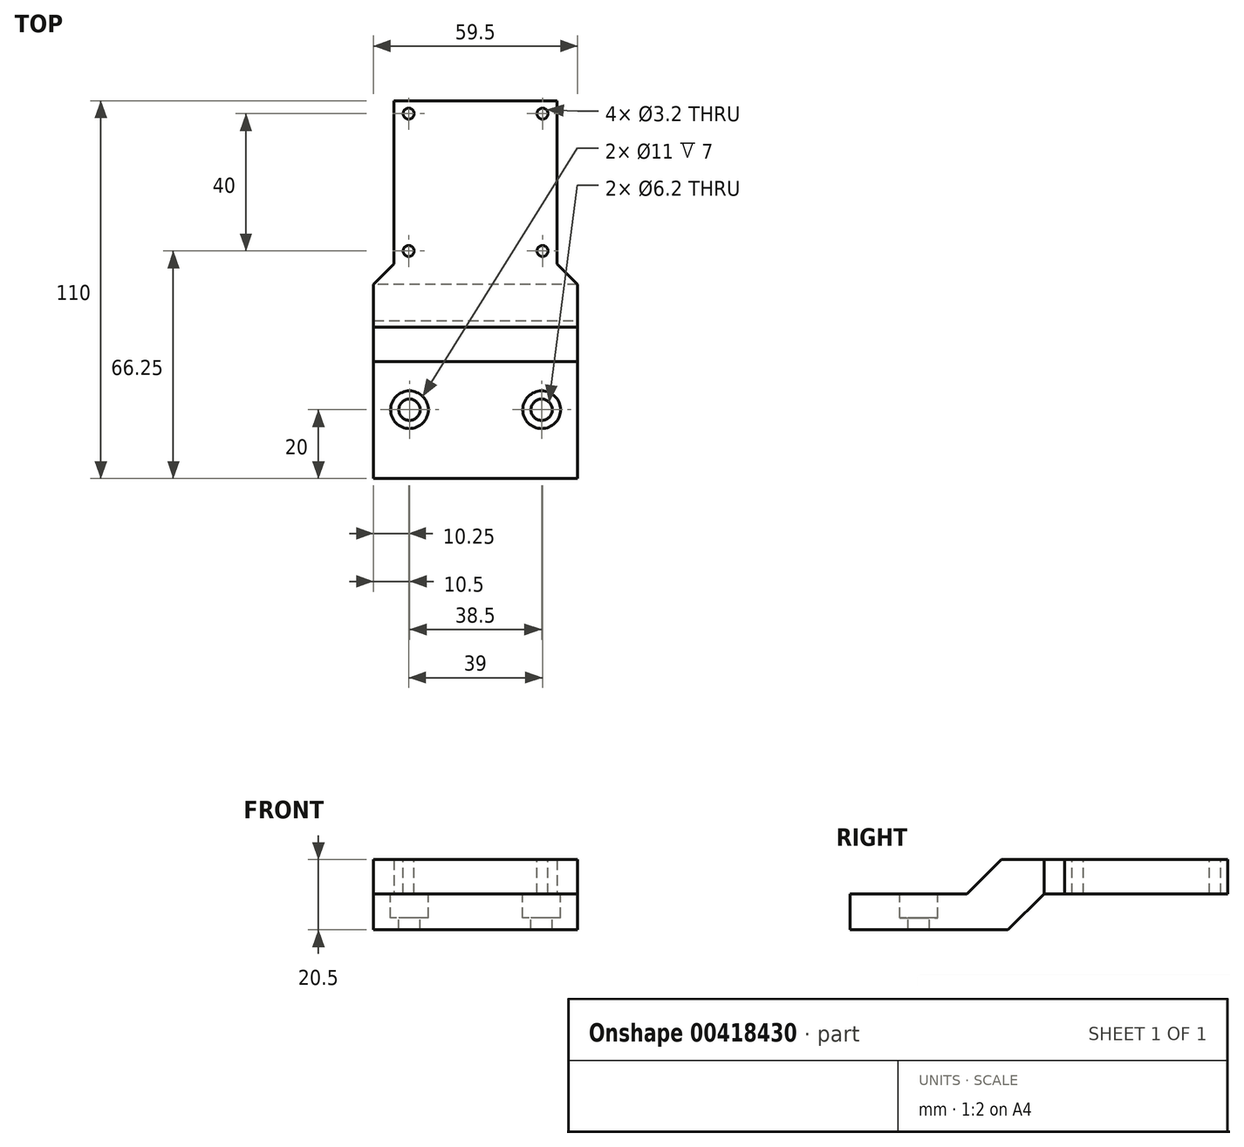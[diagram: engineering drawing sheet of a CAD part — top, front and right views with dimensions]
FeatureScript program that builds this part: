
annotation { "Feature Type Name" : "Feature", "Feature Type Description" : "" }
export const myFeature = defineFeature(function(context is Context, id is Id, definition is map)
    precondition{}
    {
        {
            var Q0;
            Q0=qCreatedBy(makeId("Top.planeOp"),FACE);
            var sketch = newSketch(context, id + "F0", { "sketchPlane" : qUnion([Q0])});
            skLineSegment(sketch, "E0.bottom", {"start": v(23.75, 23.75) * mm, "end": v(-23.75, 23.75) * mm});
            skLineSegment(sketch, "E0.left", {"start": v(23.75, 23.75) * mm, "end": v(23.75, -23.75) * mm});
            skLineSegment(sketch, "E0.right", {"start": v(-23.75, 23.75) * mm, "end": v(-23.75, -23.75) * mm});
            skPoint(sketch, "E0.middle", {"position": v(0, 0) * mm});
            skLineSegment(sketch, "E1.top", {"start": v(-29.75, -86.25) * mm, "end": v(29.75, -86.25) * mm});
            skLineSegment(sketch, "E1.left", {"start": v(-29.75, -29.75) * mm, "end": v(-29.75, -86.25) * mm});
            skLineSegment(sketch, "E1.right", {"start": v(29.75, -29.75) * mm, "end": v(29.75, -86.25) * mm});
            skLineSegment(sketch, "E2", {"start": v(-23.75, -23.75) * mm, "end": v(-29.75, -29.75) * mm});
            skLineSegment(sketch, "E3", {"start": v(23.75, -23.75) * mm, "end": v(29.75, -29.75) * mm});
            skPoint(sketch, "E4.orphan", {"position": v(-29.75, -23.75) * mm});
            skSolve(sketch);
        }
        {
            var Q0;
            Q0 = qSketchRegion(id + "F0", true);
            extrude(context, id + "F1", {"entities" : qUnion([Q0]), "depth" : 10 * mm});
        }
        {
            var Q0;
            Q0=makeQuery(id+"F1.opExtrude","CAP_FACE",FACE,{"disambiguationData":[OSD([sQuery(id+"F0.wireOp",EDGE,"E0.bottom"),sQuery(id+"F0.wireOp",EDGE,"E0.left"),sQuery(id+"F0.wireOp",EDGE,"E0.right"),sQuery(id+"F0.wireOp",EDGE,"E1.top"),sQuery(id+"F0.wireOp",EDGE,"E1.left"),sQuery(id+"F0.wireOp",EDGE,"E1.right"),sQuery(id+"F0.wireOp",EDGE,"E2"),sQuery(id+"F0.wireOp",EDGE,"E3")])],"isStart":true});
            var sketch = newSketch(context, id + "F2", { "sketchPlane" : qUnion([Q0])});
            skLineSegment(sketch, "E5", {"start": v(29.75, 86.25) * mm, "end": v(29.75, 29.75) * mm});
            skLineSegment(sketch, "E6", {"start": v(29.75, 29.75) * mm, "end": v(-29.75, 29.75) * mm});
            skLineSegment(sketch, "E7", {"start": v(-29.75, 29.75) * mm, "end": v(-29.75, 86.25) * mm});
            skLineSegment(sketch, "E8", {"start": v(-29.75, 86.25) * mm, "end": v(29.75, 86.25) * mm});
            skSolve(sketch);
        }
        {
            var Q0;
            Q0 = qSketchRegion(id + "F2", true);
            extrude(context, id + "F3", {"entities" : qUnion([Q0]), "operationType" : NewBodyOperationType.ADD, "depth" : 10.5 * mm});
        }
        {
            var Q0;
            Q0=makeQuery(id+"F3.boolean.opBoolean","MERGE",FACE,{"derivedFrom":[makeQuery(id+"F1.opExtrude","SWEPT_FACE",FACE,{"disambiguationData":[OSD([sQuery(id+"F0.wireOp",EDGE,"E1.right")])]}),makeQuery(id+"F3.opExtrude","SWEPT_FACE",FACE,{"disambiguationData":[OSD([sQuery(id+"F2.wireOp",EDGE,"E5")])]})]});
            var sketch = newSketch(context, id + "F4", { "sketchPlane" : qUnion([Q0])});
            skLineSegment(sketch, "E9", {"start": v(-42.25, 10) * mm, "end": v(-52.25, 0) * mm});
            skLineSegment(sketch, "E10", {"start": v(-52.25, 0) * mm, "end": v(-86.25, 0) * mm});
            skLineSegment(sketch, "E11", {"start": v(-86.25, 0) * mm, "end": v(-86.25, 10) * mm});
            skLineSegment(sketch, "E12", {"start": v(-29.75, 0) * mm, "end": v(-40.25, -10.5) * mm});
            skLineSegment(sketch, "E13", {"start": v(-40.25, -10.5) * mm, "end": v(-29.75, -10.5) * mm});
            skLineSegment(sketch, "E14", {"start": v(-29.75, -10.5) * mm, "end": v(-29.75, 0) * mm});
            skSolve(sketch);
        }
        {
            var Q0;
            {var subQ0=sQuery(id+"F4.wireOp",EDGE,"E9");Q0=makeQuery(id+"F4.imprint","IMPRINT",FACE,{"disambiguationData":[TD([[makeQuery(id+"F4.imprint","IMPRINT",EDGE,{"derivedFrom":subQ0}),-1.0]])]});}
            var Q1;
            Q1=makeQuery(id+"F4.imprint","IMPRINT",FACE,{"disambiguationData":[TD([[makeQuery(id+"F4.imprint","IMPRINT",EDGE,{"derivedFrom":sQuery(id+"F4.wireOp",EDGE,"E12")}),1.0]])]});
            extrude(context, id + "F5", {"entities" : qUnion([Q0, Q1]), "operationType" : NewBodyOperationType.REMOVE, "endBound" : BoundingType.THROUGH_ALL, "oppositeDirection" : true, "depth" : 25 * mm});
        }
        {
            var Q0;
            Q0=makeQuery(id+"F5.boolean.opBoolean","COPY",FACE,{"derivedFrom":makeQuery(id+"F5.opExtrude","SWEPT_FACE",FACE,{"disambiguationData":[OSD([sQuery(id+"F4.wireOp",EDGE,"E10")])]})});
            var sketch = newSketch(context, id + "F6", { "sketchPlane" : qUnion([Q0])});
            skLineSegment(sketch, "E15", {"start": v(-29.75, -66.25) * mm, "end": v(29.75, -66.25) * mm});
            skCircle(sketch, "E16", {"center": v(-19.25, -66.25) * mm, "radius": 5.5 * mm});
            skCircle(sketch, "E17", {"center": v(19.25, -66.25) * mm, "radius": 5.5 * mm});
            skSolve(sketch);
        }
        {
            var Q0;
            Q0 = qSketchRegion(id + "F6", true);
            extrude(context, id + "F7", {"entities" : qUnion([Q0]), "operationType" : NewBodyOperationType.REMOVE, "oppositeDirection" : true, "depth" : 7 * mm});
        }
        {
            var Q0;
            Q0=makeQuery(id+"F7.boolean.opBoolean","COPY",FACE,{"derivedFrom":makeQuery(id+"F7.opExtrude","CAP_FACE",FACE,{"disambiguationData":[OSD([sQuery(id+"F6.wireOp",EDGE,"E17")])],"isStart":false})});
            var sketch = newSketch(context, id + "F8", { "sketchPlane" : qUnion([Q0])});
            skCircle(sketch, "E18", {"center": v(19.25, -66.25) * mm, "radius": 3.1 * mm});
            skSolve(sketch);
        }
        {
            var Q0;
            Q0 = qSketchRegion(id + "F8", true);
            extrude(context, id + "F9", {"entities" : qUnion([Q0]), "operationType" : NewBodyOperationType.REMOVE, "endBound" : BoundingType.UP_TO_NEXT, "oppositeDirection" : true, "depth" : 25 * mm});
        }
        {
            var Q0;
            Q0=makeQuery(id+"F7.boolean.opBoolean","COPY",FACE,{"derivedFrom":makeQuery(id+"F7.opExtrude","CAP_FACE",FACE,{"disambiguationData":[OSD([sQuery(id+"F6.wireOp",EDGE,"E16")])],"isStart":false})});
            var sketch = newSketch(context, id + "F10", { "sketchPlane" : qUnion([Q0])});
            skCircle(sketch, "E19", {"center": v(-19.25, -66.25) * mm, "radius": 3.1 * mm});
            skSolve(sketch);
        }
        {
            var Q0;
            Q0 = qSketchRegion(id + "F10", true);
            extrude(context, id + "F11", {"entities" : qUnion([Q0]), "operationType" : NewBodyOperationType.REMOVE, "endBound" : BoundingType.UP_TO_NEXT, "oppositeDirection" : true, "depth" : 25 * mm});
        }
        {
            var Q0;
            Q0=makeQuery(id+"F1.opExtrude","CAP_FACE",FACE,{"disambiguationData":[OSD([sQuery(id+"F0.wireOp",EDGE,"E0.bottom"),sQuery(id+"F0.wireOp",EDGE,"E0.left"),sQuery(id+"F0.wireOp",EDGE,"E0.right"),sQuery(id+"F0.wireOp",EDGE,"E1.top"),sQuery(id+"F0.wireOp",EDGE,"E1.left"),sQuery(id+"F0.wireOp",EDGE,"E1.right"),sQuery(id+"F0.wireOp",EDGE,"E2"),sQuery(id+"F0.wireOp",EDGE,"E3")])],"isStart":false});
            var sketch = newSketch(context, id + "F12", { "sketchPlane" : qUnion([Q0])});
            skLineSegment(sketch, "E20.bottom", {"start": v(-19.5, 20) * mm, "end": v(19.5, 20) * mm});
            skLineSegment(sketch, "E20.top", {"start": v(-19.5, -20) * mm, "end": v(19.5, -20) * mm});
            skLineSegment(sketch, "E20.left", {"start": v(-19.5, 20) * mm, "end": v(-19.5, -20) * mm});
            skLineSegment(sketch, "E20.right", {"start": v(19.5, 20) * mm, "end": v(19.5, -20) * mm});
            skPoint(sketch, "E20.middle", {"position": v(0, 0) * mm});
            skCircle(sketch, "E21", {"center": v(-19.5, -20) * mm, "radius": 1.6 * mm});
            skCircle(sketch, "E22", {"center": v(-19.5, 20) * mm, "radius": 1.6 * mm});
            skCircle(sketch, "E23", {"center": v(19.5, 20) * mm, "radius": 1.6 * mm});
            skCircle(sketch, "E24", {"center": v(19.5, -20) * mm, "radius": 1.6 * mm});
            skSolve(sketch);
        }
        {
            var Q0;
            {var subQ0=sQuery(id+"F12.wireOp",EDGE,"E20.left");var subQ1=sQuery(id+"F12.wireOp",EDGE,"E20.bottom");var subQ2=makeQuery(id+"F12.imprint","INTERSECT",VERTEX,{"derivedFrom":[subQ1,subQ0]});Q0=makeQuery(id+"F12.imprint","IMPRINT",FACE,{"disambiguationData":[TD([[makeQuery(id+"F12.imprint","IMPRINT",EDGE,{"disambiguationData":[TD([[subQ2,-1.0]])],"derivedFrom":subQ1}),1.0]])]});}
            var Q1;
            {var subQ0=sQuery(id+"F12.wireOp",EDGE,"E20.left");var subQ1=sQuery(id+"F12.wireOp",EDGE,"E20.bottom");var subQ2=makeQuery(id+"F12.imprint","INTERSECT",VERTEX,{"derivedFrom":[subQ1,subQ0]});Q1=makeQuery(id+"F12.imprint","IMPRINT",FACE,{"disambiguationData":[TD([[makeQuery(id+"F12.imprint","IMPRINT",EDGE,{"disambiguationData":[TD([[subQ2,-1.0]])],"derivedFrom":subQ1}),-1.0]])]});}
            var Q2;
            {var subQ0=sQuery(id+"F12.wireOp",EDGE,"E20.right");var subQ1=sQuery(id+"F12.wireOp",EDGE,"E20.bottom");var subQ2=makeQuery(id+"F12.imprint","INTERSECT",VERTEX,{"derivedFrom":[subQ1,subQ0]});Q2=makeQuery(id+"F12.imprint","IMPRINT",FACE,{"disambiguationData":[TD([[makeQuery(id+"F12.imprint","IMPRINT",EDGE,{"disambiguationData":[TD([[subQ2,1.0]])],"derivedFrom":subQ1}),-1.0]])]});}
            var Q3;
            {var subQ0=sQuery(id+"F12.wireOp",EDGE,"E20.right");var subQ1=sQuery(id+"F12.wireOp",EDGE,"E20.bottom");var subQ2=makeQuery(id+"F12.imprint","INTERSECT",VERTEX,{"derivedFrom":[subQ1,subQ0]});Q3=makeQuery(id+"F12.imprint","IMPRINT",FACE,{"disambiguationData":[TD([[makeQuery(id+"F12.imprint","IMPRINT",EDGE,{"disambiguationData":[TD([[subQ2,1.0]])],"derivedFrom":subQ1}),1.0]])]});}
            var Q4;
            {var subQ0=sQuery(id+"F12.wireOp",EDGE,"E20.left");var subQ1=sQuery(id+"F12.wireOp",EDGE,"E20.top");var subQ2=makeQuery(id+"F12.imprint","INTERSECT",VERTEX,{"derivedFrom":[subQ1,subQ0]});Q4=makeQuery(id+"F12.imprint","IMPRINT",FACE,{"disambiguationData":[TD([[makeQuery(id+"F12.imprint","IMPRINT",EDGE,{"disambiguationData":[TD([[subQ2,-1.0]])],"derivedFrom":subQ1}),1.0]])]});}
            var Q5;
            {var subQ0=sQuery(id+"F12.wireOp",EDGE,"E20.left");var subQ1=sQuery(id+"F12.wireOp",EDGE,"E20.top");var subQ2=makeQuery(id+"F12.imprint","INTERSECT",VERTEX,{"derivedFrom":[subQ1,subQ0]});Q5=makeQuery(id+"F12.imprint","IMPRINT",FACE,{"disambiguationData":[TD([[makeQuery(id+"F12.imprint","IMPRINT",EDGE,{"disambiguationData":[TD([[subQ2,-1.0]])],"derivedFrom":subQ1}),-1.0]])]});}
            var Q6;
            {var subQ0=sQuery(id+"F12.wireOp",EDGE,"E20.right");var subQ1=sQuery(id+"F12.wireOp",EDGE,"E20.top");var subQ2=makeQuery(id+"F12.imprint","INTERSECT",VERTEX,{"derivedFrom":[subQ1,subQ0]});Q6=makeQuery(id+"F12.imprint","IMPRINT",FACE,{"disambiguationData":[TD([[makeQuery(id+"F12.imprint","IMPRINT",EDGE,{"disambiguationData":[TD([[subQ2,1.0]])],"derivedFrom":subQ1}),1.0]])]});}
            var Q7;
            {var subQ0=sQuery(id+"F12.wireOp",EDGE,"E20.right");var subQ1=sQuery(id+"F12.wireOp",EDGE,"E20.top");var subQ2=makeQuery(id+"F12.imprint","INTERSECT",VERTEX,{"derivedFrom":[subQ1,subQ0]});Q7=makeQuery(id+"F12.imprint","IMPRINT",FACE,{"disambiguationData":[TD([[makeQuery(id+"F12.imprint","IMPRINT",EDGE,{"disambiguationData":[TD([[subQ2,1.0]])],"derivedFrom":subQ1}),-1.0]])]});}
            extrude(context, id + "F13", {"entities" : qUnion([Q0, Q1, Q2, Q3, Q4, Q5, Q6, Q7]), "operationType" : NewBodyOperationType.REMOVE, "endBound" : BoundingType.UP_TO_NEXT, "oppositeDirection" : true, "depth" : 25 * mm});
        }
    });
